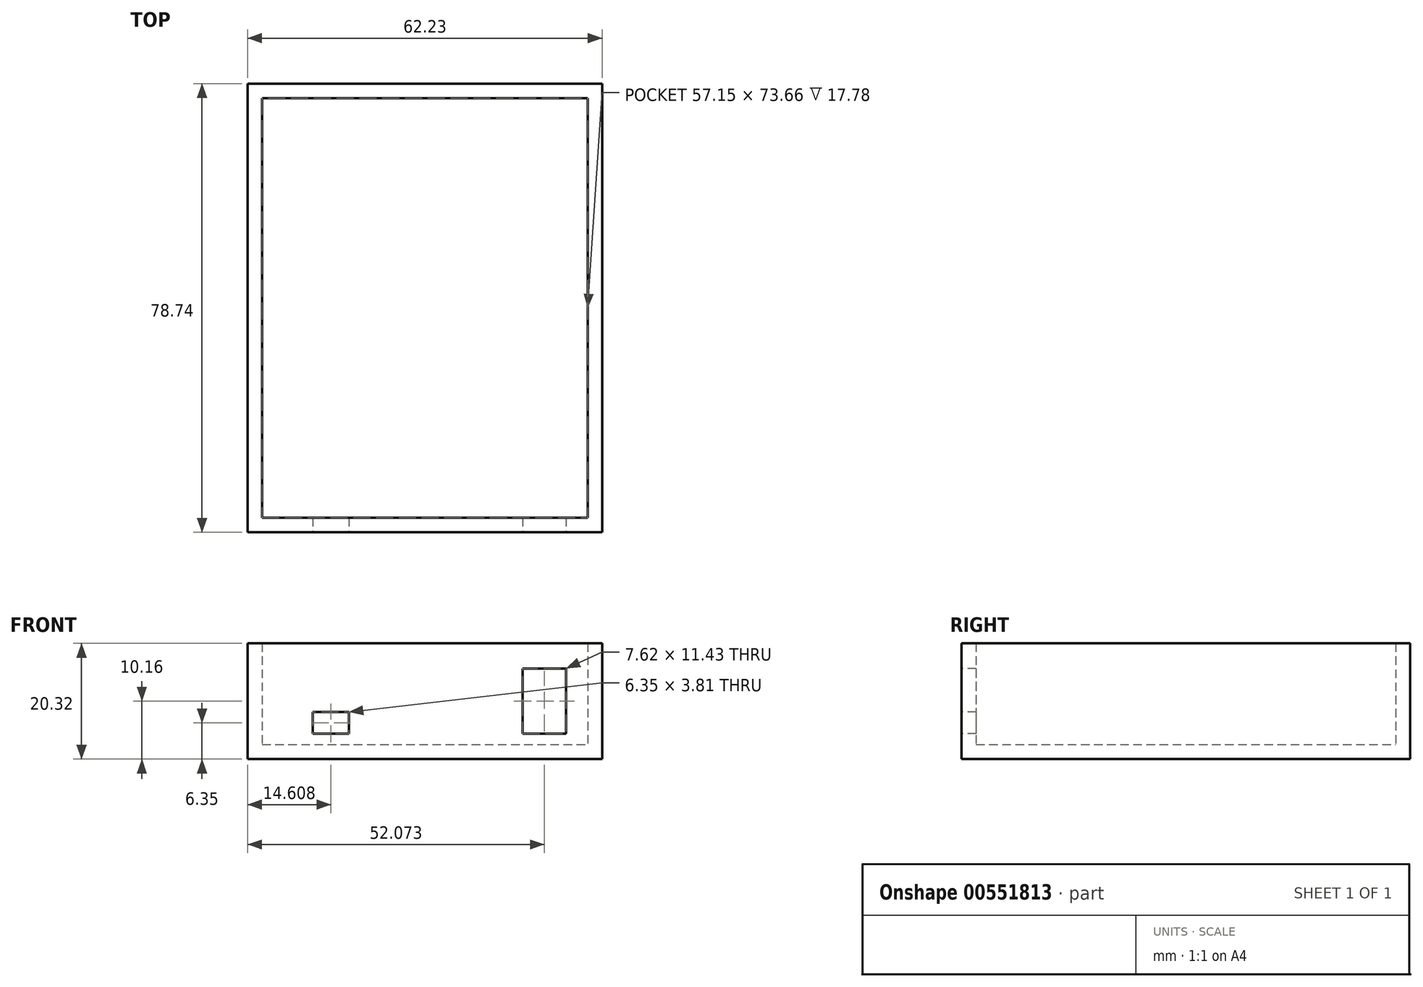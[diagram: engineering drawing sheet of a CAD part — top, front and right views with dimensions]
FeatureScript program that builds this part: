
annotation { "Feature Type Name" : "Feature", "Feature Type Description" : "" }
export const myFeature = defineFeature(function(context is Context, id is Id, definition is map)
    precondition{}
    {
        {
            var Q0;
            Q0=qCreatedBy(makeId("Front.planeOp"),FACE);
            var sketch = newSketch(context, id + "F0", { "sketchPlane" : qUnion([Q0])});
            skLineSegment(sketch, "E0.bottom", {"start": v(-31.59, 10.16) * mm, "end": v(30.64, 10.16) * mm});
            skLineSegment(sketch, "E0.top", {"start": v(-31.59, -10.16) * mm, "end": v(30.64, -10.16) * mm});
            skLineSegment(sketch, "E0.left", {"start": v(-31.59, 10.16) * mm, "end": v(-31.59, -10.16) * mm});
            skLineSegment(sketch, "E0.right", {"start": v(30.64, 10.16) * mm, "end": v(30.64, -10.16) * mm});
            skPoint(sketch, "E0.middle", {"position": v(-0.47, 0) * mm});
            skSolve(sketch);
        }
        {
            var Q0;
            Q0 = qSketchRegion(id + "F0", true);
            extrude(context, id + "F1", {"entities" : qUnion([Q0]), "endBound" : BoundingType.SYMMETRIC, "depth" : 78.74 * mm, "offsetDistance" : 25.4 * mm});
        }
        {
            var Q0;
            Q0=makeQuery(id+"F1.opExtrude","SWEPT_FACE",FACE,{"disambiguationData":[OSD([sQuery(id+"F0.wireOp",EDGE,"E0.bottom")])]});
            shell(context, id + "F2", {"entities" : qUnion([Q0]), "thickness" : 2.54 * mm});
        }
        {
            var Q0;
            Q0=makeQuery(id+"F1.opExtrude","CAP_FACE",FACE,{"disambiguationData":[OSD([sQuery(id+"F0.wireOp",EDGE,"E0.bottom"),sQuery(id+"F0.wireOp",EDGE,"E0.top"),sQuery(id+"F0.wireOp",EDGE,"E0.left"),sQuery(id+"F0.wireOp",EDGE,"E0.right")])],"isStart":false});
            var sketch = newSketch(context, id + "F3", { "sketchPlane" : qUnion([Q0])});
            skLineSegment(sketch, "E1.bottom", {"start": v(24.3, 5.72) * mm, "end": v(16.67, 5.72) * mm});
            skLineSegment(sketch, "E1.top", {"start": v(24.3, -5.71) * mm, "end": v(16.67, -5.71) * mm});
            skLineSegment(sketch, "E1.left", {"start": v(24.3, 5.72) * mm, "end": v(24.3, -5.71) * mm});
            skLineSegment(sketch, "E1.right", {"start": v(16.67, 5.72) * mm, "end": v(16.67, -5.71) * mm});
            skPoint(sketch, "E1.middle", {"position": v(20.48, 0) * mm});
            skLineSegment(sketch, "E2.bottom", {"start": v(-20.16, -1.9) * mm, "end": v(-13.8, -1.9) * mm});
            skLineSegment(sketch, "E2.top", {"start": v(-20.16, -5.72) * mm, "end": v(-13.8, -5.72) * mm});
            skLineSegment(sketch, "E2.left", {"start": v(-20.16, -1.9) * mm, "end": v(-20.16, -5.72) * mm});
            skLineSegment(sketch, "E2.right", {"start": v(-13.8, -1.9) * mm, "end": v(-13.8, -5.72) * mm});
            skSolve(sketch);
        }
        {
            var Q0;
            Q0=makeQuery(id+"F3.imprint","IMPRINT",FACE,{"disambiguationData":[TD([[makeQuery(id+"F3.imprint","IMPRINT",EDGE,{"derivedFrom":sQuery(id+"F3.wireOp",EDGE,"E2.bottom")}),-1.0]])]});
            var Q1;
            Q1=makeQuery(id+"F3.imprint","IMPRINT",FACE,{"disambiguationData":[TD([[makeQuery(id+"F3.imprint","IMPRINT",EDGE,{"derivedFrom":sQuery(id+"F3.wireOp",EDGE,"E1.bottom")}),1.0]])]});
            extrude(context, id + "F4", {"entities" : qUnion([Q0, Q1]), "operationType" : NewBodyOperationType.REMOVE, "oppositeDirection" : true, "depth" : 25.4 * mm, "offsetDistance" : 25.4 * mm});
        }
    });
